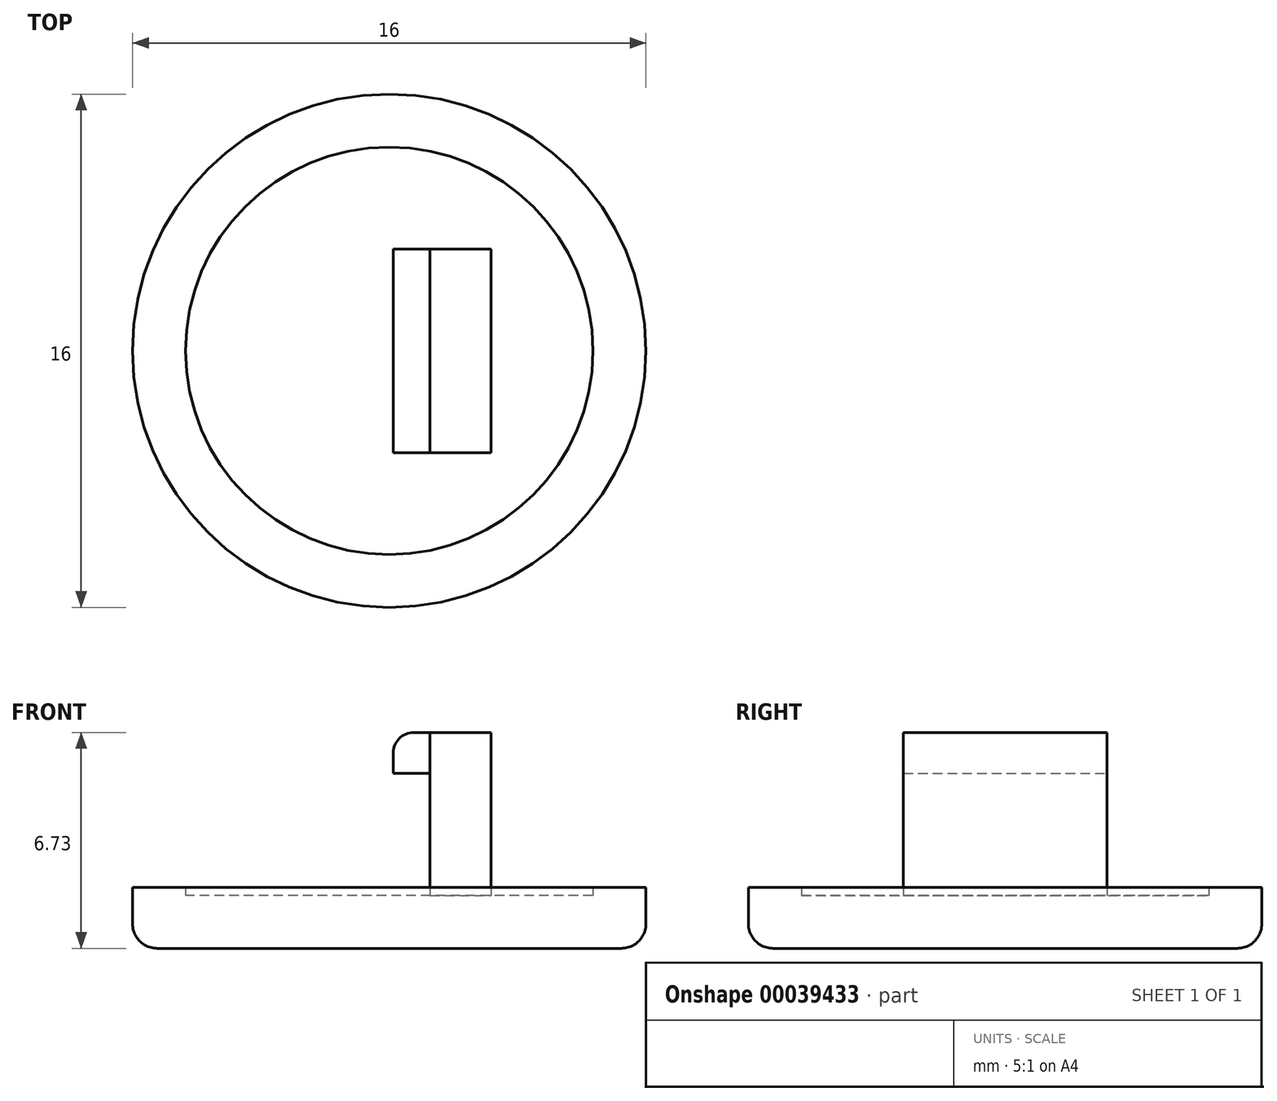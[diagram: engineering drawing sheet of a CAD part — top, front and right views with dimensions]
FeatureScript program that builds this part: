
annotation { "Feature Type Name" : "Feature", "Feature Type Description" : "" }
export const myFeature = defineFeature(function(context is Context, id is Id, definition is map)
    precondition{}
    {
        {
            var Q0;
            Q0=qCreatedBy(makeId("Top.planeOp"),FACE);
            var sketch = newSketch(context, id + "F0", { "sketchPlane" : qUnion([Q0])});
            skCircle(sketch, "E0", {"center": v(0, 0) * mm, "radius": 8 * mm});
            skSolve(sketch);
        }
        {
            var Q0;
            Q0=makeQuery(id+"F0.imprint","IMPRINT",FACE,{"disambiguationData":[TD([[makeQuery(id+"F0.imprint","IMPRINT",EDGE,{"derivedFrom":sQuery(id+"F0.wireOp",EDGE,"E0")}),1.0]])]});
            extrude(context, id + "F1", {"entities" : qUnion([Q0]), "depth" : 1.9 * mm});
        }
        {
            var Q0;
            Q0=makeQuery(id+"F1.opExtrude","CAP_FACE",FACE,{"disambiguationData":[OSD([sQuery(id+"F0.wireOp",EDGE,"E0")])],"isStart":false});
            shell(context, id + "F2", {"entities" : qUnion([Q0]), "thickness" : 1.65 * mm});
        }
        {
            var Q0;
            {var subQ0=sQuery(id+"F0.wireOp",EDGE,"E0");Q0=makeQuery(id+"F2.opShell","OFFSET_FACE",FACE,{"disambiguationData":[OSD([subQ0]),TDD([makeQuery(id+"F1.opExtrude","CAP_FACE",FACE,{"disambiguationData":[OSD([subQ0])],"isStart":true})])]});}
            var sketch = newSketch(context, id + "F3", { "sketchPlane" : qUnion([Q0])});
            skLineSegment(sketch, "E1.rect.bottom", {"start": v(-3.17, -3.18) * mm, "end": v(3.18, -3.17) * mm});
            skLineSegment(sketch, "E1.rect.top", {"start": v(-3.18, 3.18) * mm, "end": v(3.17, 3.18) * mm});
            skLineSegment(sketch, "E1.rect.left", {"start": v(-3.17, -3.18) * mm, "end": v(-3.18, 3.17) * mm});
            skLineSegment(sketch, "E1.rect.right", {"start": v(3.18, -3.17) * mm, "end": v(3.17, 3.18) * mm});
            skPoint(sketch, "E1.rect.middle", {"position": v(0, 0) * mm});
            skLineSegment(sketch, "E2.bottom", {"start": v(-3.17, -3.18) * mm, "end": v(-1.27, -3.17) * mm});
            skLineSegment(sketch, "E2.top", {"start": v(-3.18, 3.18) * mm, "end": v(-1.27, 3.18) * mm});
            skLineSegment(sketch, "E2.right", {"start": v(-1.27, -3.17) * mm, "end": v(-1.27, 3.18) * mm});
            skLineSegment(sketch, "E3", {"start": v(0, 3.17) * mm, "end": v(0, -3.17) * mm, "construction": true});
            skLineSegment(sketch, "E4.MirrorCS", {"start": v(1.27, -3.17) * mm, "end": v(1.27, 3.18) * mm});
            skSolve(sketch);
        }
        {
            var Q0;
            {var subQ2=sQuery(id+"F3.wireOp",EDGE,"E1.rect.right");Q0=makeQuery(id+"F3.imprint","IMPRINT",FACE,{"disambiguationData":[TD([[makeQuery(id+"F3.imprint","IMPRINT",EDGE,{"derivedFrom":subQ2}),1.0]])]});}
            var Q1;
            Q1=makeQuery(id+"F3.imprint","IMPRINT",FACE,{"disambiguationData":[TD([[makeQuery(id+"F3.imprint","IMPRINT",EDGE,{"derivedFrom":sQuery(id+"F3.wireOp",EDGE,"E2.bottom")}),1.0]])]});
            extrude(context, id + "F7", {"entities" : qUnion([Q0, Q1]), "operationType" : NewBodyOperationType.ADD, "depth" : 5.08 * mm});
        }
        {
            var Q0;
            Q0=makeQuery(id+"F7.opExtrude","CAP_FACE",FACE,{"disambiguationData":[OSD([sQuery(id+"F3.wireOp",EDGE,"E1.rect.bottom"),sQuery(id+"F3.wireOp",EDGE,"E1.rect.top"),sQuery(id+"F3.wireOp",EDGE,"E1.rect.right"),sQuery(id+"F3.wireOp",EDGE,"E4.MirrorCS")])],"isStart":false});
            var sketch = newSketch(context, id + "F8", { "sketchPlane" : qUnion([Q0])});
            skLineSegment(sketch, "E5.bottom", {"start": v(1.27, -3.17) * mm, "end": v(0.13, -3.17) * mm});
            skLineSegment(sketch, "E5.top", {"start": v(1.27, 3.18) * mm, "end": v(0.13, 3.18) * mm});
            skLineSegment(sketch, "E5.left", {"start": v(1.27, -3.17) * mm, "end": v(1.27, 3.18) * mm});
            skLineSegment(sketch, "E5.right", {"start": v(0.13, -3.17) * mm, "end": v(0.13, 3.18) * mm});
            skSolve(sketch);
        }
        {
            var Q0;
            Q0=makeQuery(id+"F7.opExtrude","CAP_FACE",FACE,{"disambiguationData":[OSD([sQuery(id+"F3.wireOp",EDGE,"E2.bottom"),sQuery(id+"F3.wireOp",EDGE,"E2.top"),sQuery(id+"F3.wireOp",EDGE,"E1.rect.left"),sQuery(id+"F3.wireOp",EDGE,"E2.right")])],"isStart":false});
            var sketch = newSketch(context, id + "F4", { "sketchPlane" : qUnion([Q0])});
            skLineSegment(sketch, "E6.bottom", {"start": v(-1.27, -3.17) * mm, "end": v(-0.13, -3.17) * mm});
            skLineSegment(sketch, "E6.top", {"start": v(-1.27, 3.18) * mm, "end": v(-0.13, 3.18) * mm});
            skLineSegment(sketch, "E6.left", {"start": v(-1.27, -3.17) * mm, "end": v(-1.27, 3.18) * mm});
            skLineSegment(sketch, "E6.right", {"start": v(-0.13, -3.17) * mm, "end": v(-0.13, 3.18) * mm});
            skSolve(sketch);
        }
        {
            var Q0;
            Q0=makeQuery(id+"F8.imprint","IMPRINT",FACE,{"disambiguationData":[TD([[makeQuery(id+"F8.imprint","IMPRINT",EDGE,{"derivedFrom":sQuery(id+"F8.wireOp",EDGE,"E5.bottom")}),-1.0]])]});
            var Q1;
            Q1=makeQuery(id+"F4.imprint","IMPRINT",FACE,{"disambiguationData":[TD([[makeQuery(id+"F4.imprint","IMPRINT",EDGE,{"derivedFrom":sQuery(id+"F4.wireOp",EDGE,"E6.bottom")}),1.0]])]});
            extrude(context, id + "F9", {"entities" : qUnion([Q0, Q1]), "oppositeDirection" : true, "depth" : 1.27 * mm});
        }
        {
            var Q0;
            Q0=makeQuery(id+"F1.opExtrude","CAP_EDGE",EDGE,{"disambiguationData":[OSD([sQuery(id+"F0.wireOp",EDGE,"E0")])],"isStart":true});
            fillet(context, id + "F5", {"entities" : qUnion([Q0]), "radius" : 0.76 * mm, "tangentPropagation" : true, "allowEdgeOverflow" : false});
        }
        {
            var Q0;
            Q0=makeQuery(id+"F9.opExtrude","CAP_EDGE",EDGE,{"disambiguationData":[OSD([sQuery(id+"F4.wireOp",EDGE,"E6.right")])],"isStart":true});
            var Q1;
            Q1=makeQuery(id+"F9.opExtrude","CAP_EDGE",EDGE,{"disambiguationData":[OSD([sQuery(id+"F8.wireOp",EDGE,"E5.right")])],"isStart":true});
            fillet(context, id + "F6", {"entities" : qUnion([Q0, Q1]), "radius" : 0.64 * mm, "tangentPropagation" : true, "allowEdgeOverflow" : false});
        }
    });
